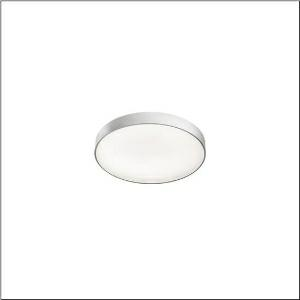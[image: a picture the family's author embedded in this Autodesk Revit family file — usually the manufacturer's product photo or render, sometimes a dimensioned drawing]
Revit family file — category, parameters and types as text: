
# Revit family: round_21_s_51mr34nd0421s
name_source: partatom
category: Lighting Fixtures
units: mm (PartAtom-declared; Revit-internal decimal feet)

## family parameters
Cut with Voids When Loaded = No
Host = Face
Light Source = No
Part Type = Normal
Room Calculation Point = No
Round Connector Dimension = Use Diameter
Shared = No

## types (1)
- Round 21 S (1 x LED, 3810 lm, 28.3 W, 4000K)
    Apparent Load = 28 VA
    CIE Flux Codes = 66 90 98 71 100
    Color Rendering = 80
    Color Temperature = 4000K
    Default Elevation = 1800 mm
    Description = Round 21 S, wall and ceiling luminaire, primary optical cover: micro prismatic cover, of PMMA, transparent, CAT 2 (L<= 3000cd/m²), light emission: direct/indirect distribution, primary light characteristic: symmetric, installation type: surface-mounted, suspended mounting, LED, rated luminous flux: 3.800lm, luminous efficacy: 135lm/W, light colour: 840, colour temperature: 4000K, control gear: DALI 2, with terminal, 5-pole, mains connection: 230V, AC, 50/60Hz, rated input power: 28.3W, housing, of aluminium, coated, silver, diameter: 400mm, height: 62mm, protection rating (complete): IP40, insulation class (complete): insulation class I (protective earthing), certification: CE, impact resistance: IK04, permissible operating ambient temperature: -10..+35°C, packaging unit: 1 piece
    Height = 87 mm
    Lamp = 1 x LED
    Lamp Light Flux = 3810 lm
    Lamp Power = 28.3 W
    Lamp count = 1
    Length = 400 mm
    Luminous efficacy = 135 lm/W
    Manufacturer = Siteco
    ModVariant = No
    Model = 51MR34ND0421S
    Mounting Place = Ceiling
    Mounting Type = Surface mounted
    Number of Poles = 1
    OnlyDefault = Yes
    Power Factor = 1
    Product Name = Round 21 S
    Product group = wall and ceiling luminaire
    ProductGroupID = 304
    Protection Class = Protection class I
    Protection Degree = IP 40
    RLX_Detail_Level = 1
    RLX_Emergency_Light_Flux = 0 lm
    RLX_Emergency_Type = 0
    RLX_Emergency_Type_DB = No
    RlxData = <blob elided: 15133 chars, md5=b3cbd813>
    Socket = socket
    Standby Power = 0 W
    System Light Flux = 3810 lm
    System Power = 28 W
    Type Comments = Product without accessories
    Type Image = l_1258336.jpg
    URL = http://relux.com
    VarID = ---
    Voltage = 0 V
    Weight = 0.00 kg
    Width = 0 mm  [stored 0 ft]

note: [stored X ft] marks values corroborated as IEEE doubles in the binary element streams (Revit-internal decimal feet)

## geometry (parser evidence)
native form markers: Sweep x13
no freeform markers — native parametric forms only
